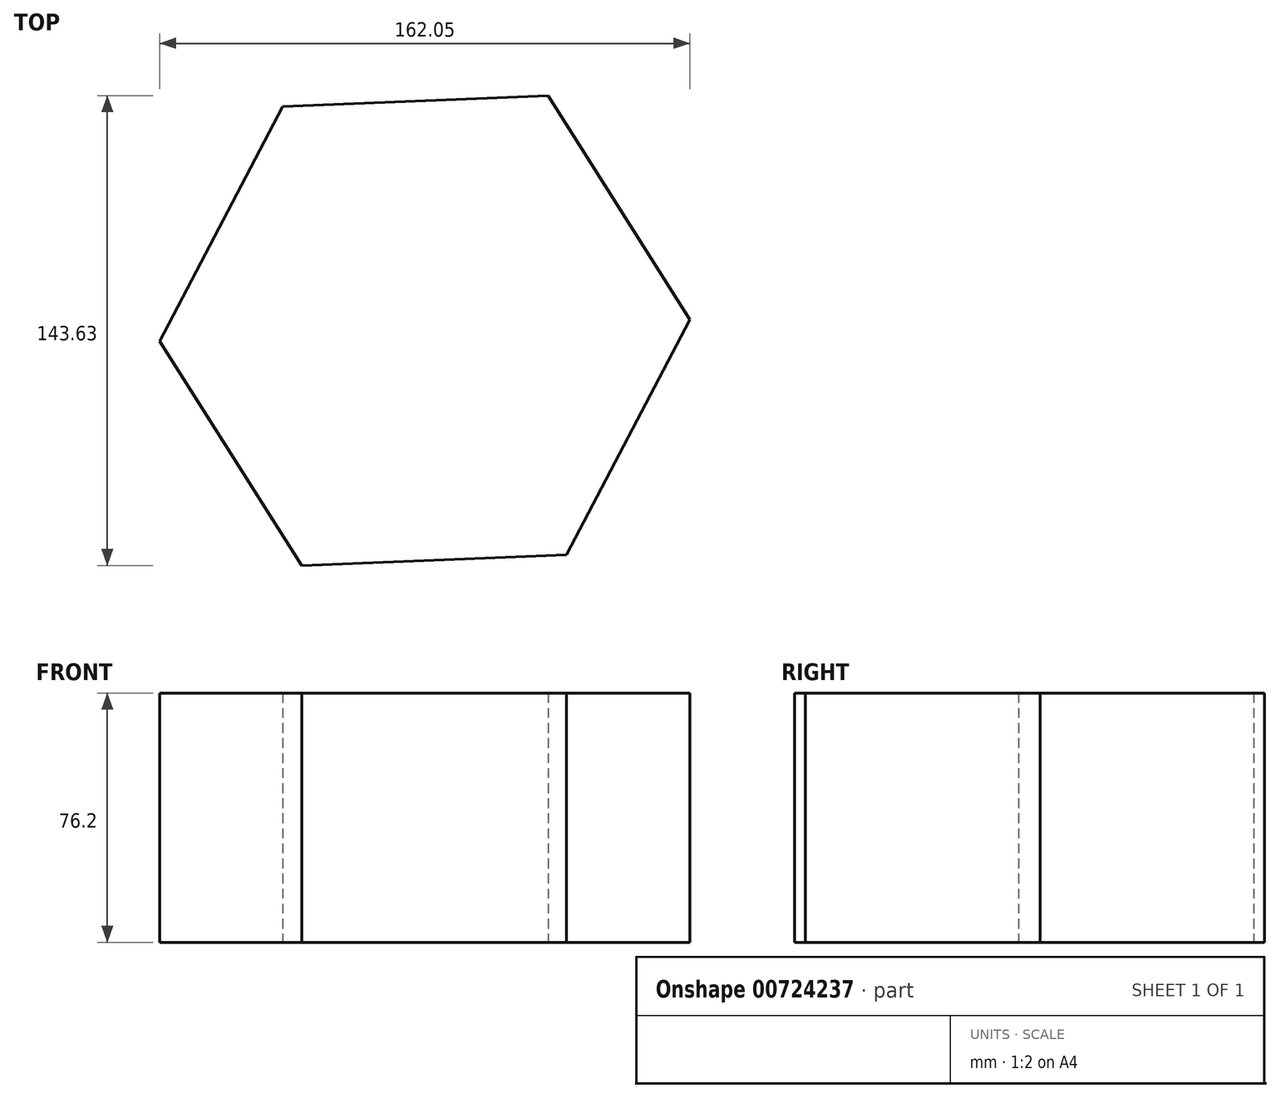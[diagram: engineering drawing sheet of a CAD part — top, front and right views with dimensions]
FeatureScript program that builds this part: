
annotation { "Feature Type Name" : "Feature", "Feature Type Description" : "" }
export const myFeature = defineFeature(function(context is Context, id is Id, definition is map)
    precondition{}
    {
        {
            var Q0;
            Q0=qCreatedBy(makeId("Top.planeOp"),FACE);
            var sketch = newSketch(context, id + "F0", { "sketchPlane" : qUnion([Q0])});
            skCircle(sketch, "E0.cCircle", {"center": v(-70.5, 8.3) * mm, "radius": 70.23 * mm, "construction": true});
            skLineSegment(sketch, "E0.0", {"start": v(10.53, 11.6) * mm, "end": v(-27.13, -60.22) * mm});
            skLineSegment(sketch, "E0.1", {"start": v(-27.13, -60.22) * mm, "end": v(-108.15, -63.51) * mm});
            skLineSegment(sketch, "E0.2", {"start": v(-108.15, -63.51) * mm, "end": v(-151.52, 5) * mm});
            skLineSegment(sketch, "E0.3", {"start": v(-151.52, 5) * mm, "end": v(-113.86, 76.82) * mm});
            skLineSegment(sketch, "E0.4", {"start": v(-113.86, 76.82) * mm, "end": v(-32.84, 80.12) * mm});
            skLineSegment(sketch, "E0.5", {"start": v(-32.84, 80.12) * mm, "end": v(10.53, 11.6) * mm});
            skPoint(sketch, "E0.0.midPoint", {"position": v(-8.3, -24.3) * mm});
            skSolve(sketch);
        }
        {
            var Q0;
            Q0=makeQuery(id+"F0.imprint","IMPRINT",FACE,{"disambiguationData":[TD([[makeQuery(id+"F0.imprint","IMPRINT",EDGE,{"derivedFrom":sQuery(id+"F0.wireOp",EDGE,"E0.0")}),-1.0]])]});
            extrude(context, id + "F1", {"entities" : qUnion([Q0]), "depth" : 76.2 * mm, "offsetDistance" : 25.4 * mm});
        }
    });
